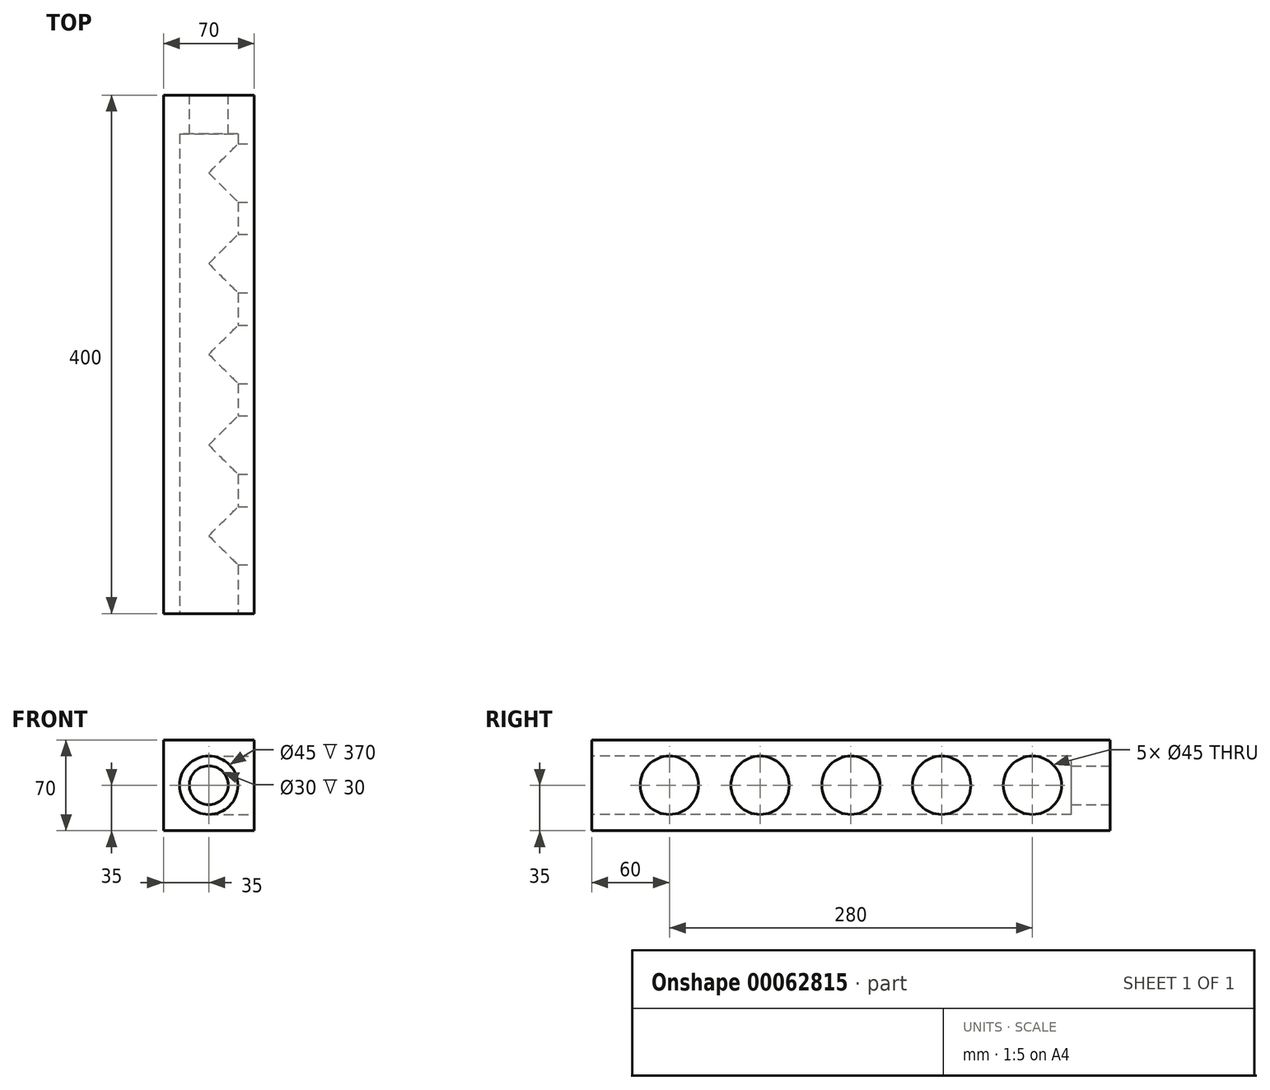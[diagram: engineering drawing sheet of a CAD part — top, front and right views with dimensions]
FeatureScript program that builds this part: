
annotation { "Feature Type Name" : "Feature", "Feature Type Description" : "" }
export const myFeature = defineFeature(function(context is Context, id is Id, definition is map)
    precondition{}
    {
        {
            var Q0;
            Q0=qCreatedBy(makeId("Front.planeOp"),FACE);
            var sketch = newSketch(context, id + "F0", { "sketchPlane" : qUnion([Q0])});
            skLineSegment(sketch, "E0.rect.bottom", {"start": v(35, -35) * mm, "end": v(-35, -35) * mm});
            skLineSegment(sketch, "E0.rect.top", {"start": v(35, 35) * mm, "end": v(-35, 35) * mm});
            skLineSegment(sketch, "E0.rect.left", {"start": v(35, -35) * mm, "end": v(35, 35) * mm});
            skLineSegment(sketch, "E0.rect.right", {"start": v(-35, -35) * mm, "end": v(-35, 35) * mm});
            skPoint(sketch, "E0.rect.middle", {"position": v(0, 0) * mm});
            skSolve(sketch);
        }
        {
            var Q0;
            Q0 = qSketchRegion(id + "F0", true);
            extrude(context, id + "F1", {"entities" : qUnion([Q0]), "depth" : 400 * mm});
        }
        {
            var Q0;
            Q0=makeQuery(id+"F1.opExtrude","SWEPT_FACE",FACE,{"disambiguationData":[OSD([sQuery(id+"F0.wireOp",EDGE,"E0.rect.left")])]});
            var sketch = newSketch(context, id + "F2", { "sketchPlane" : qUnion([Q0])});
            skCircle(sketch, "E1", {"center": v(-340, 0) * mm, "radius": 22.5 * mm});
            skCircle(sketch, "E2", {"center": v(-270, 0) * mm, "radius": 22.5 * mm});
            skCircle(sketch, "E3", {"center": v(-200, 0) * mm, "radius": 22.5 * mm});
            skCircle(sketch, "E4", {"center": v(-130, 0) * mm, "radius": 22.5 * mm});
            skCircle(sketch, "E5", {"center": v(-60, 0) * mm, "radius": 22.5 * mm});
            skSolve(sketch);
        }
        {
            var Q0;
            Q0 = qSketchRegion(id + "F2", true);
            extrude(context, id + "F3", {"entities" : qUnion([Q0]), "operationType" : NewBodyOperationType.REMOVE, "oppositeDirection" : true, "depth" : 35 * mm});
        }
        {
            var Q0;
            Q0=makeQuery(id+"F1.opExtrude","CAP_FACE",FACE,{"disambiguationData":[OSD([sQuery(id+"F0.wireOp",EDGE,"E0.rect.bottom"),sQuery(id+"F0.wireOp",EDGE,"E0.rect.top"),sQuery(id+"F0.wireOp",EDGE,"E0.rect.left"),sQuery(id+"F0.wireOp",EDGE,"E0.rect.right")])],"isStart":false});
            var sketch = newSketch(context, id + "F4", { "sketchPlane" : qUnion([Q0])});
            skCircle(sketch, "E6", {"center": v(0, 0) * mm, "radius": 22.5 * mm});
            skSolve(sketch);
        }
        {
            var Q0;
            Q0 = qSketchRegion(id + "F4", true);
            extrude(context, id + "F5", {"entities" : qUnion([Q0]), "operationType" : NewBodyOperationType.REMOVE, "oppositeDirection" : true, "depth" : 370 * mm});
        }
        {
            var Q0;
            Q0=makeQuery(id+"F1.opExtrude","CAP_FACE",FACE,{"disambiguationData":[OSD([sQuery(id+"F0.wireOp",EDGE,"E0.rect.bottom"),sQuery(id+"F0.wireOp",EDGE,"E0.rect.top"),sQuery(id+"F0.wireOp",EDGE,"E0.rect.left"),sQuery(id+"F0.wireOp",EDGE,"E0.rect.right")])],"isStart":true});
            var sketch = newSketch(context, id + "F6", { "sketchPlane" : qUnion([Q0])});
            skCircle(sketch, "E7", {"center": v(0, 0) * mm, "radius": 15 * mm});
            skSolve(sketch);
        }
        {
            var Q0;
            Q0 = qSketchRegion(id + "F6", true);
            extrude(context, id + "F7", {"entities" : qUnion([Q0]), "operationType" : NewBodyOperationType.REMOVE, "oppositeDirection" : true, "depth" : 45 * mm});
        }
    });
